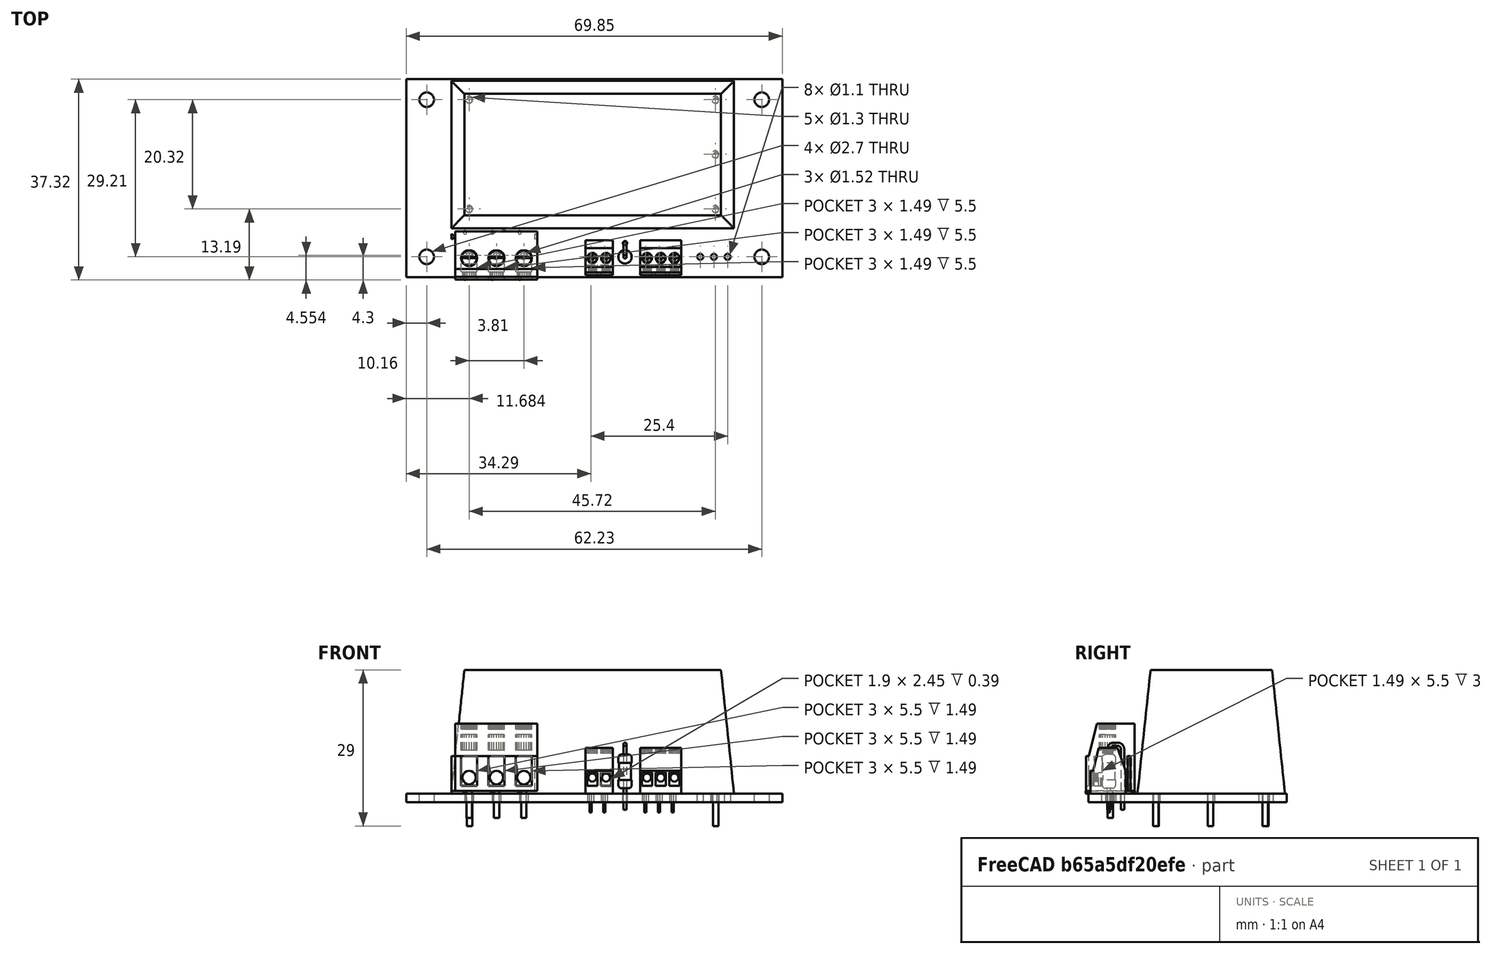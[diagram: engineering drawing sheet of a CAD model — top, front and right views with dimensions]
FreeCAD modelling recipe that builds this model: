
FCSTD DOCUMENT  (FreeCAD 0.19R24276 (Git))
Label: power supply
License: All rights reserved
LicenseURL: http://en.wikipedia.org/wiki/All_rights_reserved
objects: Part::Feature×6, App::Part×4, PartDesign::CoordinateSystem×1, Sketcher::SketchObject×1, App::Link×1
note: 8 computed .brp shape members not serialized (recipe doc carries the construction recipe); baked Part::Feature solids carry a one-line shape summary decoded from their .brp

FEATURE [PartDesign::CoordinateSystem] Local_CS_7c43
  AttacherType = Attacher::AttachEngine3D
FEATURE [Part::Feature] Pcb_7c43
  shape: bbox 69.85 x 36.83 x 1.6 mm, 28 faces (baked)
FEATURE [Sketcher::SketchObject] PCB_Sketch_7c43
  FullyConstrained = false
  sketch-geometry (4):
    g0: LineSegment StartX=140.97 StartY=-33.02 StartZ=0 EndX=140.97 EndY=3.81 EndZ=0
    g1: LineSegment StartX=210.82 StartY=-33.02 StartZ=0 EndX=140.97 EndY=-33.02 EndZ=0
    g2: LineSegment StartX=210.82 StartY=3.81 StartZ=0 EndX=210.82 EndY=-33.02 EndZ=0
    g3: LineSegment StartX=140.97 StartY=3.81 StartZ=0 EndX=210.82 EndY=3.81 EndZ=0
  constraints (4):
    c: Coincident(g0,g1)
    c: Coincident(g0,g3)
    c: Coincident(g1,g2)
    c: Coincident(g2,g3)
FEATURE [App::Part] Board_Geoms_7c43
  Group = -> [Local_CS_7c43,Pcb_7c43,PCB_Sketch_7c43]
  Origin = -> Origin
FEATURE [Part::Feature] Shape  label="PS1_Fusion_60E0183C"
  Placement = pos=(152.654,0,0) rot=(0,0,1;0rad)
  shape: bbox 52.5 x 27.4 x 29 mm, 16 faces (baked)
FEATURE [Part::Feature] Shape001  label="R1_R_Axial_DIN0207_L63mm_D25mm_P254mm_Vertical_60E01AFD"
  Placement = pos=(181.61,-29.21,0) rot=(0,0,1;1.5708rad)
  shape: bbox 2.706 x 4.292 x 12.6 mm, 17 faces (baked)
FEATURE [Part::Feature] Shape002  label="J4_TerminalBlock_1x02_P2_54mm_Horizontal_60DF7D87[2]"
  Placement = pos=(175.26,-29.21,0) rot=(0,0,1;0rad)
  shape: bbox 5.08 x 6.5 x 12 mm, 313 faces, 5 solids (baked)
FEATURE [Part::Feature] Shape003  label="J3_TerminalBlock_1x03_P2_54mm_Horizontal_60DF7D67"
  Placement = pos=(185.42,-29.21,0) rot=(0,0,1;0rad)
  shape: bbox 7.62 x 6.5 x 12 mm, 465 faces, 7 solids (baked)
FEATURE [App::Link] J3_TerminalBlock_1x03_P2_54mm_Horizontal_60DF7D67_ln_  label="J2_TerminalBlock_1x03_P2_54mm_Horizontal_60E01A2D"
  LinkPlacement = pos=(195.58,-29.21,0) rot=(0,0,1;0rad)
  LinkedObject = -> Shape003
  Placement = pos=(195.58,-29.21,0) rot=(0,0,1;0rad)
FEATURE [Part::Feature] Shape004  label="J1_OSTTA03416_60DF7D1F"
  Placement = pos=(152.654,-28.956,0) rot=(0,0,1;0rad)
  shape: bbox 15.94 x 9.1 x 17.5 mm, 576 faces (baked)
FEATURE [App::Part] Top_7c43
  Group = -> [Shape,Shape001,Shape002,Shape003,J3_TerminalBlock_1x03_P2_54mm_Horizontal_60DF7D67_ln_,Shape004]
  Origin = -> Origin003
FEATURE [App::Part] Step_Models_7c43
  Group = -> [Top_7c43]
  Origin = -> Origin002
FEATURE [App::Part] Board_7c43  label="power_supply"
  Group = -> [Board_Geoms_7c43,Step_Models_7c43]
  Origin = -> Origin001
